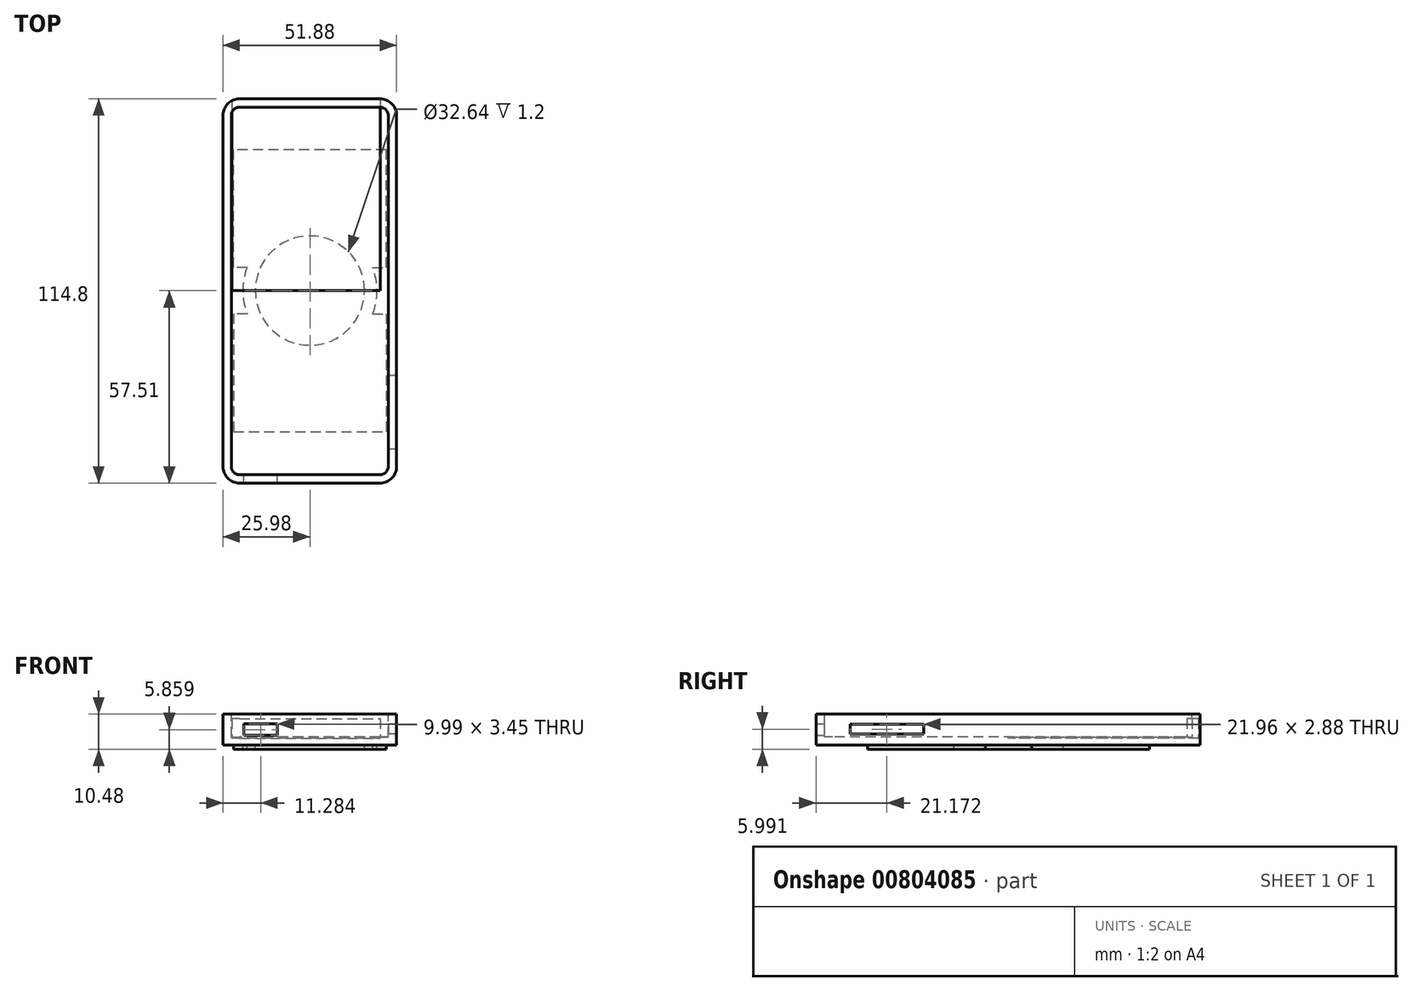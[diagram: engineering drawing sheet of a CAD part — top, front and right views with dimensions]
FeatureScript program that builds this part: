
annotation { "Feature Type Name" : "Feature", "Feature Type Description" : "" }
export const myFeature = defineFeature(function(context is Context, id is Id, definition is map)
    precondition{}
    {
        {
            var Q0;
            Q0=qCreatedBy(makeId("Top.planeOp"),FACE);
            var sketch = newSketch(context, id + "F0", { "sketchPlane" : qUnion([Q0])});
            skLineSegment(sketch, "E0", {"start": v(25.9, 57.29) * mm, "end": v(25.9, -57.51) * mm});
            skLineSegment(sketch, "E1", {"start": v(25.9, -57.51) * mm, "end": v(-25.98, -57.51) * mm});
            skLineSegment(sketch, "E2", {"start": v(-25.98, -57.51) * mm, "end": v(-25.98, 57.29) * mm});
            skLineSegment(sketch, "E3", {"start": v(-25.98, 57.29) * mm, "end": v(25.9, 57.29) * mm});
            skSolve(sketch);
        }
        {
            var Q0;
            Q0 = qSketchRegion(id + "F0", true);
            extrude(context, id + "F1", {"entities" : qUnion([Q0]), "depth" : 9.28 * mm, "offsetDistance" : 25 * mm});
        }
        {
            var Q0;
            Q0=makeQuery(id+"F1.opExtrude","SWEPT_EDGE",EDGE,{"disambiguationData":[OSD([sQuery(id+"F0.wireOp",EDGE,"E0"),sQuery(id+"F0.wireOp",EDGE,"E3")])]});
            var Q1;
            Q1=makeQuery(id+"F1.opExtrude","SWEPT_EDGE",EDGE,{"disambiguationData":[OSD([sQuery(id+"F0.wireOp",EDGE,"E0"),sQuery(id+"F0.wireOp",EDGE,"E1")])]});
            var Q2;
            Q2=makeQuery(id+"F1.opExtrude","SWEPT_EDGE",EDGE,{"disambiguationData":[OSD([sQuery(id+"F0.wireOp",EDGE,"E2"),sQuery(id+"F0.wireOp",EDGE,"E3")])]});
            var Q3;
            Q3=makeQuery(id+"F1.opExtrude","SWEPT_EDGE",EDGE,{"disambiguationData":[OSD([sQuery(id+"F0.wireOp",EDGE,"E1"),sQuery(id+"F0.wireOp",EDGE,"E2")])]});
            fillet(context, id + "F2", {"entities" : qUnion([Q0, Q1, Q2, Q3]), "radius" : 5 * mm, "tangentPropagation" : true, "allowEdgeOverflow" : false});
        }
        {
            var Q0;
            Q0=makeQuery(id+"F1.opExtrude","CAP_FACE",FACE,{"disambiguationData":[OSD([sQuery(id+"F0.wireOp",EDGE,"E0"),sQuery(id+"F0.wireOp",EDGE,"E1"),sQuery(id+"F0.wireOp",EDGE,"E2"),sQuery(id+"F0.wireOp",EDGE,"E3")])],"isStart":false});
            shell(context, id + "F3", {"entities" : qUnion([Q0]), "thickness" : 2.5 * mm});
        }
        {
            var Q0;
            Q0=qCreatedBy(makeId("Front.planeOp"),FACE);
            var sketch = newSketch(context, id + "F4", { "sketchPlane" : qUnion([Q0])});
            skLineSegment(sketch, "E4.bottom", {"start": v(-19.7, 2.93) * mm, "end": v(-9.7, 2.93) * mm});
            skLineSegment(sketch, "E4.top", {"start": v(-19.7, 6.38) * mm, "end": v(-9.7, 6.38) * mm});
            skLineSegment(sketch, "E4.left", {"start": v(-19.7, 2.93) * mm, "end": v(-19.7, 6.38) * mm});
            skLineSegment(sketch, "E4.right", {"start": v(-9.7, 2.93) * mm, "end": v(-9.7, 6.38) * mm});
            skSolve(sketch);
        }
        {
            var Q0;
            Q0 = qSketchRegion(id + "F4", true);
            extrude(context, id + "F5", {"entities" : qUnion([Q0]), "operationType" : NewBodyOperationType.REMOVE, "depth" : 69.5 * mm, "offsetDistance" : 25 * mm});
        }
        {
            var Q0;
            Q0=qCreatedBy(makeId("Right.planeOp"),FACE);
            var sketch = newSketch(context, id + "F6", { "sketchPlane" : qUnion([Q0])});
            skLineSegment(sketch, "E5.bottom", {"start": v(-47.32, 3.35) * mm, "end": v(-25.36, 3.35) * mm});
            skLineSegment(sketch, "E5.top", {"start": v(-47.32, 6.23) * mm, "end": v(-25.36, 6.23) * mm});
            skLineSegment(sketch, "E5.left", {"start": v(-47.32, 3.35) * mm, "end": v(-47.32, 6.23) * mm});
            skLineSegment(sketch, "E5.right", {"start": v(-25.36, 3.35) * mm, "end": v(-25.36, 6.23) * mm});
            skSolve(sketch);
        }
        {
            var Q0;
            Q0 = qSketchRegion(id + "F6", true);
            extrude(context, id + "F7", {"entities" : qUnion([Q0]), "operationType" : NewBodyOperationType.REMOVE, "depth" : 36.6 * mm, "offsetDistance" : 25 * mm});
        }
        {
            var Q0;
            Q0=qCreatedBy(makeId("Front.planeOp"),FACE);
            var sketch = newSketch(context, id + "F8", { "sketchPlane" : qUnion([Q0])});
            skLineSegment(sketch, "E6.bottom", {"start": v(21.06, 2.02) * mm, "end": v(-23.25, 2.02) * mm});
            skLineSegment(sketch, "E6.top", {"start": v(21.06, 7.86) * mm, "end": v(-23.25, 7.86) * mm});
            skLineSegment(sketch, "E6.left", {"start": v(21.06, 2.02) * mm, "end": v(21.06, 7.86) * mm});
            skLineSegment(sketch, "E6.right", {"start": v(-23.25, 2.02) * mm, "end": v(-23.25, 7.86) * mm});
            skSolve(sketch);
        }
        {
            var Q0;
            Q0 = qSketchRegion(id + "F8", true);
            extrude(context, id + "F9", {"entities" : qUnion([Q0]), "operationType" : NewBodyOperationType.REMOVE, "oppositeDirection" : true, "depth" : 65.7 * mm, "offsetDistance" : 25 * mm});
        }
        {
            var Q0;
            Q0=qCreatedBy(makeId("Top.planeOp"),FACE);
            var sketch = newSketch(context, id + "F10", { "sketchPlane" : qUnion([Q0])});
            skCircle(sketch, "E7", {"center": v(0, 0) * mm, "radius": 20.02 * mm});
            skCircle(sketch, "E8.0", {"center": v(0, 0) * mm, "radius": 16.32 * mm});
            skLineSegment(sketch, "E9", {"start": v(-18.78, -6.93) * mm, "end": v(-22.8, -6.93) * mm});
            skLineSegment(sketch, "E10", {"start": v(-22.8, -6.93) * mm, "end": v(-22.8, -42.12) * mm});
            skLineSegment(sketch, "E11", {"start": v(-22.8, -42.12) * mm, "end": v(0, -42.12) * mm});
            skLineSegment(sketch, "E12.1.0", {"start": v(22.8, 42.12) * mm, "end": v(0, 42.12) * mm});
            skLineSegment(sketch, "E12.1.1", {"start": v(22.8, 6.93) * mm, "end": v(22.8, 42.12) * mm});
            skLineSegment(sketch, "E12.1.2", {"start": v(18.78, 6.93) * mm, "end": v(22.8, 6.93) * mm});
            skLineSegment(sketch, "E13", {"start": v(18.78, -6.93) * mm, "end": v(22.8, -6.93) * mm});
            skLineSegment(sketch, "E14", {"start": v(22.8, -6.93) * mm, "end": v(22.8, -42.12) * mm});
            skLineSegment(sketch, "E15", {"start": v(22.8, -42.12) * mm, "end": v(0, -42.12) * mm});
            skLineSegment(sketch, "E16.1.0", {"start": v(-22.8, 42.12) * mm, "end": v(0, 42.12) * mm});
            skLineSegment(sketch, "E16.1.1", {"start": v(-22.8, 6.93) * mm, "end": v(-22.8, 42.12) * mm});
            skLineSegment(sketch, "E16.1.2", {"start": v(-18.78, 6.93) * mm, "end": v(-22.8, 6.93) * mm});
            skSolve(sketch);
        }
        {
            var Q0;
            Q0 = qSketchRegion(id + "F10", true);
            extrude(context, id + "F11", {"entities" : qUnion([Q0]), "operationType" : NewBodyOperationType.ADD, "oppositeDirection" : true, "depth" : 1.2 * mm, "offsetDistance" : 25 * mm});
        }
    });
